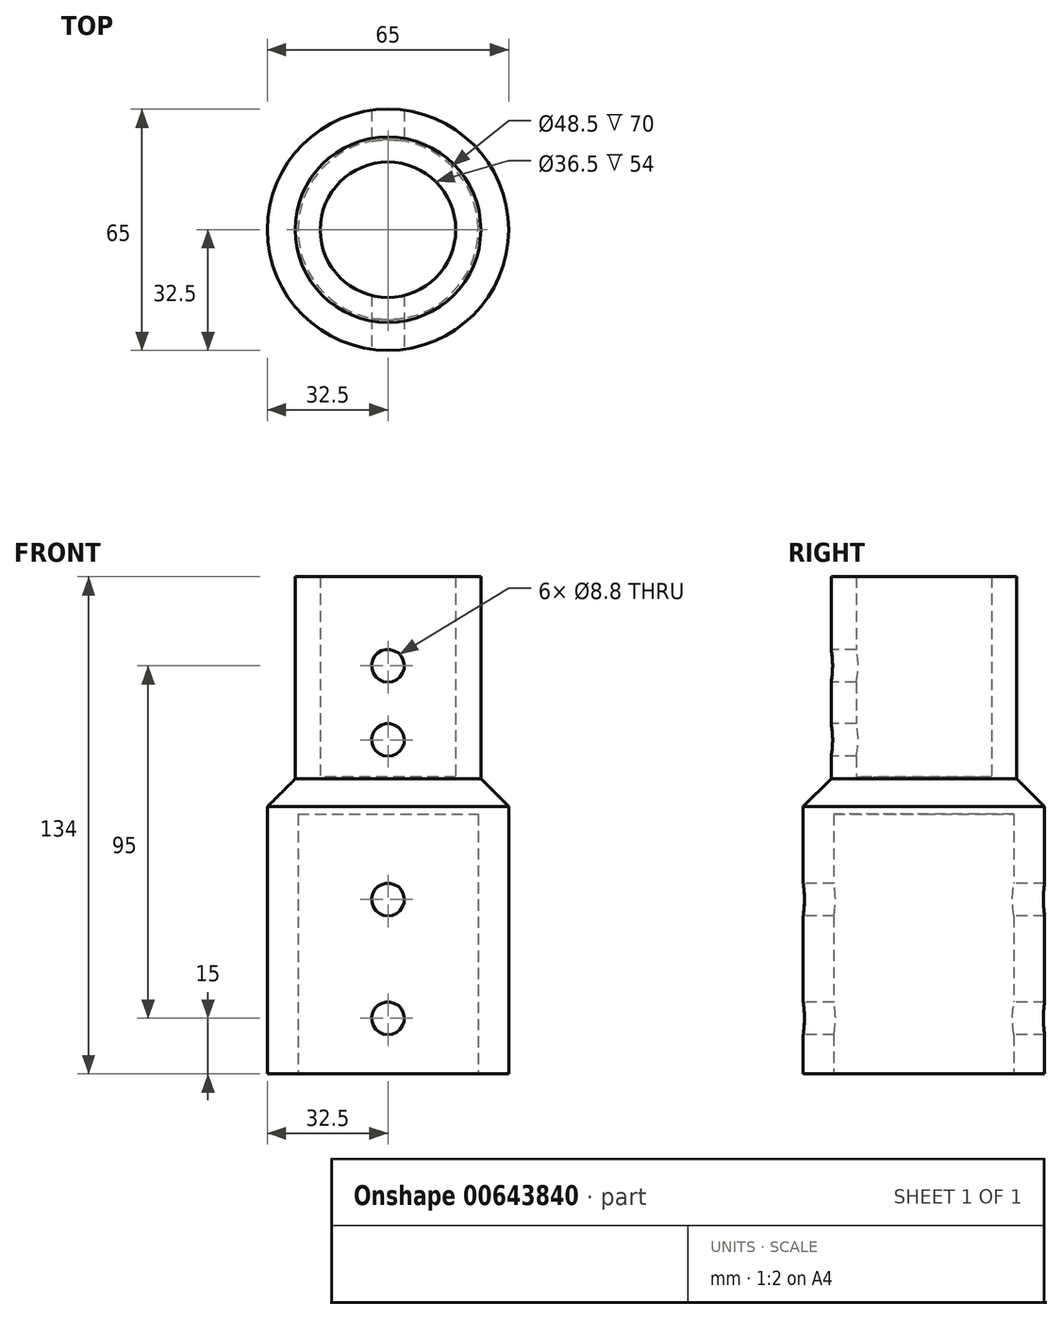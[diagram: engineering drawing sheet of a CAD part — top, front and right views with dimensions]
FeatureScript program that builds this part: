
annotation { "Feature Type Name" : "Feature", "Feature Type Description" : "" }
export const myFeature = defineFeature(function(context is Context, id is Id, definition is map)
    precondition{}
    {
        {
            var Q0;
            Q0=qCreatedBy(makeId("Top.planeOp"),FACE);
            var sketch = newSketch(context, id + "F0", { "sketchPlane" : qUnion([Q0])});
            skCircle(sketch, "E0", {"center": v(0, 0) * mm, "radius": 25 * mm});
            skCircle(sketch, "E1", {"center": v(0, 0) * mm, "radius": 18.25 * mm});
            skSolve(sketch);
        }
        {
            var Q0;
            Q0 = qSketchRegion(id + "F0", true);
            extrude(context, id + "F1", {"entities" : qUnion([Q0]), "depth" : 54 * mm, "offsetDistance" : 25 * mm});
        }
        {
            var Q0;
            Q0=qCreatedBy(makeId("Front.planeOp"),FACE);
            cPlane(context, id + "F2", {"entities" : qUnion([Q0]), "cplaneType" : CPlaneType.OFFSET, "offset" : 26 * mm, "width" : 150 * mm, "height" : 150 * mm});
        }
        {
            var Q0;
            Q0=qCreatedBy(id+"F2.planeOp",FACE);
            var sketch = newSketch(context, id + "F3", { "sketchPlane" : qUnion([Q0])});
            skPoint(sketch, "E2", {"position": v(0, 30) * mm});
            skPoint(sketch, "E3", {"position": v(0, 10) * mm});
            skSolve(sketch);
        }
        {
            var Q0;
            Q0=sQuery(id+"F3.wireOp",VERTEX,"E3");
            var Q1;
            Q1=sQuery(id+"F3.wireOp",VERTEX,"E2");
            var Q2;
            Q2=makeQuery(id+"F1.opExtrude","SWEPT_BODY",BODY,{"disambiguationData":[OSD([sQuery(id+"F0.wireOp",EDGE,"E0"),sQuery(id+"F0.wireOp",EDGE,"E1")])]});
            hole(context, id + "F4", {"style" : HoleStyle.SIMPLE, "endStyle" : HoleEndStyle.BLIND, "standardTappedOrClearance" : lookupTablePath({ "standard" : "ISO", "fit" : "Normal", "size" : "M8", "type" : "Clearance" }), "standardBlindInLast" : lookupTablePath({ "fit" : "Standard", "standard" : "ISO", "size" : "M8", "type" : "Clearance" }), "holeDiameter" : 8.8 * mm, "majorDiameter" : 5 * mm, "holeDepth" : 15.75 * mm, "isTappedThrough" : true, "tappedDepth" : 12 * mm, "tapClearance" : 3, "locations" : qUnion([Q0, Q1]), "scope" : qUnion([Q2])});
        }
        {
            var Q0;
            Q0=makeQuery(id+"F0.imprint","IMPRINT",FACE,{"disambiguationData":[TD([[makeQuery(id+"F0.imprint","IMPRINT",EDGE,{"derivedFrom":sQuery(id+"F0.wireOp",EDGE,"E0")}),1.0]])]});
            var sketch = newSketch(context, id + "F5", { "sketchPlane" : qUnion([Q0])});
            skCircle(sketch, "E4", {"center": v(0, 0) * mm, "radius": 32.5 * mm});
            skSolve(sketch);
        }
        {
            var Q0;
            Q0 = qSketchRegion(id + "F5", true);
            extrude(context, id + "F6", {"entities" : qUnion([Q0]), "operationType" : NewBodyOperationType.ADD, "oppositeDirection" : true, "depth" : 80 * mm, "offsetDistance" : 25 * mm});
        }
        {
            var Q0;
            Q0=makeQuery(id+"F6.opExtrude","CAP_FACE",FACE,{"disambiguationData":[OSD([sQuery(id+"F5.wireOp",EDGE,"E4")])],"isStart":false});
            var sketch = newSketch(context, id + "F7", { "sketchPlane" : qUnion([Q0])});
            skCircle(sketch, "E5", {"center": v(0, 0) * mm, "radius": 24.25 * mm});
            skSolve(sketch);
        }
        {
            var Q0;
            Q0 = qSketchRegion(id + "F7", true);
            extrude(context, id + "F8", {"entities" : qUnion([Q0]), "operationType" : NewBodyOperationType.REMOVE, "oppositeDirection" : true, "depth" : 70 * mm, "offsetDistance" : 25 * mm});
        }
        {
            var Q0;
            Q0=makeQuery(id+"F6.opExtrude","CAP_EDGE",EDGE,{"disambiguationData":[OSD([sQuery(id+"F5.wireOp",EDGE,"E4")])],"isStart":true});
            chamfer(context, id + "F9", {"entities" : qUnion([Q0]), "width" : 8 * mm, "tangentPropagation" : true});
        }
        {
            var Q0;
            Q0=qCreatedBy(id+"F2.planeOp",FACE);
            cPlane(context, id + "F10", {"entities" : qUnion([Q0]), "cplaneType" : CPlaneType.OFFSET, "offset" : 25 * mm, "width" : 150 * mm, "height" : 150 * mm});
        }
        {
            var Q0;
            Q0=qCreatedBy(id+"F10.planeOp",FACE);
            var sketch = newSketch(context, id + "F11", { "sketchPlane" : qUnion([Q0])});
            skPoint(sketch, "E6", {"position": v(0, -65) * mm});
            skPoint(sketch, "E7", {"position": v(0, -33) * mm});
            skSolve(sketch);
        }
        {
            var Q0;
            Q0=sQuery(id+"F11.wireOp",VERTEX,"E7");
            var Q1;
            Q1=sQuery(id+"F11.wireOp",VERTEX,"E6");
            var Q2;
            Q2=makeQuery(id+"F1.opExtrude","SWEPT_BODY",BODY,{"disambiguationData":[OSD([sQuery(id+"F0.wireOp",EDGE,"E0"),sQuery(id+"F0.wireOp",EDGE,"E1")])]});
            hole(context, id + "F12", {"style" : HoleStyle.SIMPLE, "endStyle" : HoleEndStyle.THROUGH, "standardTappedOrClearance" : lookupTablePath({ "standard" : "ISO", "fit" : "Normal", "size" : "M8", "type" : "Clearance" }), "standardBlindInLast" : lookupTablePath({ "fit" : "Standard", "standard" : "ISO", "size" : "M8", "type" : "Clearance" }), "holeDiameter" : 8.8 * mm, "majorDiameter" : 5 * mm, "isTappedThrough" : true, "tappedDepth" : 12 * mm, "tapClearance" : 3, "locations" : qUnion([Q0, Q1]), "scope" : qUnion([Q2])});
        }
    });
